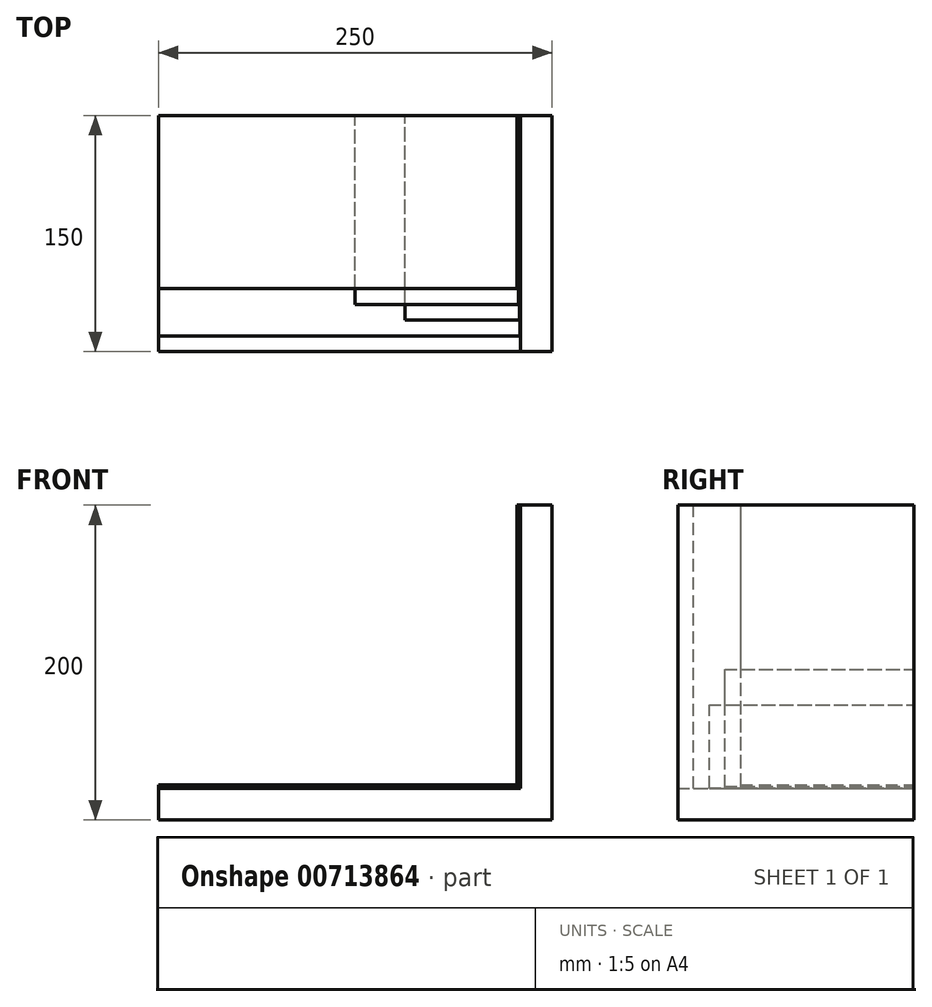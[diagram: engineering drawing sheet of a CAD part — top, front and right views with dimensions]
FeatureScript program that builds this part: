
annotation { "Feature Type Name" : "Feature", "Feature Type Description" : "" }
export const myFeature = defineFeature(function(context is Context, id is Id, definition is map)
    precondition{}
    {
        {
            var Q0;
            Q0=qCreatedBy(makeId("Front.planeOp"),FACE);
            var sketch = newSketch(context, id + "F0", { "sketchPlane" : qUnion([Q0])});
            skLineSegment(sketch, "E0", {"start": v(-201.96, -38.42) * mm, "end": v(28.04, -38.42) * mm});
            skLineSegment(sketch, "E1", {"start": v(28.04, -38.42) * mm, "end": v(28.04, 141.58) * mm});
            skLineSegment(sketch, "E2", {"start": v(28.04, 141.58) * mm, "end": v(48.04, 141.58) * mm});
            skLineSegment(sketch, "E3", {"start": v(48.04, 141.58) * mm, "end": v(48.04, -58.42) * mm});
            skLineSegment(sketch, "E4", {"start": v(48.04, -58.42) * mm, "end": v(-201.96, -58.42) * mm});
            skLineSegment(sketch, "E5", {"start": v(-201.96, -58.42) * mm, "end": v(-201.96, -38.42) * mm});
            skLineSegment(sketch, "E6", {"start": v(-201.96, -38.42) * mm, "end": v(-201.96, -38.22) * mm});
            skLineSegment(sketch, "E7", {"start": v(-201.96, -38.22) * mm, "end": v(27.84, -38.22) * mm});
            skLineSegment(sketch, "E8", {"start": v(27.84, -38.22) * mm, "end": v(27.84, 141.58) * mm});
            skLineSegment(sketch, "E9", {"start": v(27.84, 141.58) * mm, "end": v(28.04, 141.58) * mm});
            skLineSegment(sketch, "E10", {"start": v(-45.25, -38.22) * mm, "end": v(-45.25, -37.92) * mm});
            skLineSegment(sketch, "E11", {"start": v(-45.25, -37.92) * mm, "end": v(27.54, -37.92) * mm});
            skLineSegment(sketch, "E12", {"start": v(27.54, -37.92) * mm, "end": v(27.54, 14.73) * mm});
            skLineSegment(sketch, "E13", {"start": v(27.54, 14.73) * mm, "end": v(27.84, 14.73) * mm});
            skLineSegment(sketch, "E14", {"start": v(-76.99, -38.22) * mm, "end": v(-76.99, -37.22) * mm});
            skLineSegment(sketch, "E15", {"start": v(-76.99, -37.22) * mm, "end": v(26.84, -37.22) * mm});
            skLineSegment(sketch, "E16", {"start": v(26.84, -37.22) * mm, "end": v(26.84, 37.17) * mm});
            skLineSegment(sketch, "E17", {"start": v(26.84, 37.17) * mm, "end": v(27.84, 37.17) * mm});
            skLineSegment(sketch, "E18", {"start": v(-201.96, -38.22) * mm, "end": v(-201.96, -36.22) * mm});
            skLineSegment(sketch, "E19", {"start": v(-201.96, -36.22) * mm, "end": v(25.84, -36.22) * mm});
            skLineSegment(sketch, "E20", {"start": v(25.84, -36.22) * mm, "end": v(25.84, 141.58) * mm});
            skLineSegment(sketch, "E21", {"start": v(25.84, 141.58) * mm, "end": v(27.84, 141.58) * mm});
            skSolve(sketch);
        }
        {
            var Q0;
            Q0=makeQuery(id+"F0.imprint","IMPRINT",FACE,{"disambiguationData":[TD([[makeQuery(id+"F0.imprint","IMPRINT",EDGE,{"derivedFrom":sQuery(id+"F0.wireOp",EDGE,"E0")}),-1.0]])]});
            extrude(context, id + "F1", {"entities" : qUnion([Q0]), "depth" : 150 * mm});
        }
        {
            var Q0;
            Q0=makeQuery(id+"F0.imprint","IMPRINT",FACE,{"disambiguationData":[TD([[makeQuery(id+"F0.imprint","IMPRINT",EDGE,{"derivedFrom":sQuery(id+"F0.wireOp",EDGE,"E0")}),1.0]])]});
            extrude(context, id + "F2", {"entities" : qUnion([Q0]), "depth" : 140 * mm});
        }
        {
            var Q0;
            {var subQ4=sQuery(id+"F0.wireOp",EDGE,"E10");Q0=makeQuery(id+"F0.imprint","IMPRINT",FACE,{"disambiguationData":[TD([[makeQuery(id+"F0.imprint","IMPRINT",EDGE,{"derivedFrom":subQ4}),-1.0]])]});}
            extrude(context, id + "F3", {"entities" : qUnion([Q0]), "depth" : 130 * mm});
        }
        {
            var Q0;
            {var subQ0=sQuery(id+"F0.wireOp",EDGE,"E10");Q0=makeQuery(id+"F0.imprint","IMPRINT",FACE,{"disambiguationData":[TD([[makeQuery(id+"F0.imprint","IMPRINT",EDGE,{"derivedFrom":subQ0}),1.0]])]});}
            extrude(context, id + "F4", {"entities" : qUnion([Q0]), "depth" : 120 * mm});
        }
        {
            var Q0;
            {var subQ0=sQuery(id+"F0.wireOp",EDGE,"E14");Q0=makeQuery(id+"F0.imprint","IMPRINT",FACE,{"disambiguationData":[TD([[makeQuery(id+"F0.imprint","IMPRINT",EDGE,{"derivedFrom":subQ0}),1.0]])]});}
            extrude(context, id + "F5", {"entities" : qUnion([Q0]), "depth" : 110 * mm});
        }
    });
